# Revit family: ADB Electric cooktops cupboard 800
name_source: partatom
category: Equipement spécialisé
units: mm (PartAtom-declared; Revit-internal decimal feet)

## family parameters
Basée sur le plan de construction = Non
Conserver l'orientation des annotations = Non
Cote de connecteur circulaire = Utiliser le diamètre
Couper avec des vides une fois chargée = Non
Numéro OmniClass = 23.40.40.14.17.11
Partagée = Non
Repère de localisation dans la pièce = Non
Titre OmniClass = Cookers, Ovens, Stoves
Toujours verticalement = Oui
Type d'élément = Normal

## types (2) — shared parameters
C = 400 mm  [stored 1.31234 ft]
Commentaires du type = Ambassade range - Cupboards - Electric cooktops
D = 765 mm  [stored 2.50984 ft]
Fabricant = Société Industrielle de Lacanche
URL = https://www.ambassade-de-bourgogne.com
URL Cutsheet = https://www.ambassade-de-bourgogne.com
zero-valued in all types: Elévation par défaut

## per-type parameters (varying)
| type | Description | E | Electric power | Electrical Remarks | Operational Current | Poids base | Table | VTR |
| CME 840 VTR | Radiant ring electric cupboard 3,5kW+1,2kW+2,1kW+1,4/2,1kW | Non | 8900 W | 230V(MONO) ou 400V(TRI) | 39 A | 65.00 kg | 4 foyers radiants | Oui |
| CME 840 E | Hotplate electric cupboard 2x2kW+2,6kW+1,5kW | Oui | 8100 W | 230V(MONO) commutable 400V(TRI), 400V TRI sans neutre en option | 35 A | 83.00 kg | 4 plaques électriques | Non |

note: column(s) folded — value = type name in every type: Modèle

note: [stored X ft] marks values corroborated as IEEE doubles in the binary element streams (Revit-internal decimal feet)
